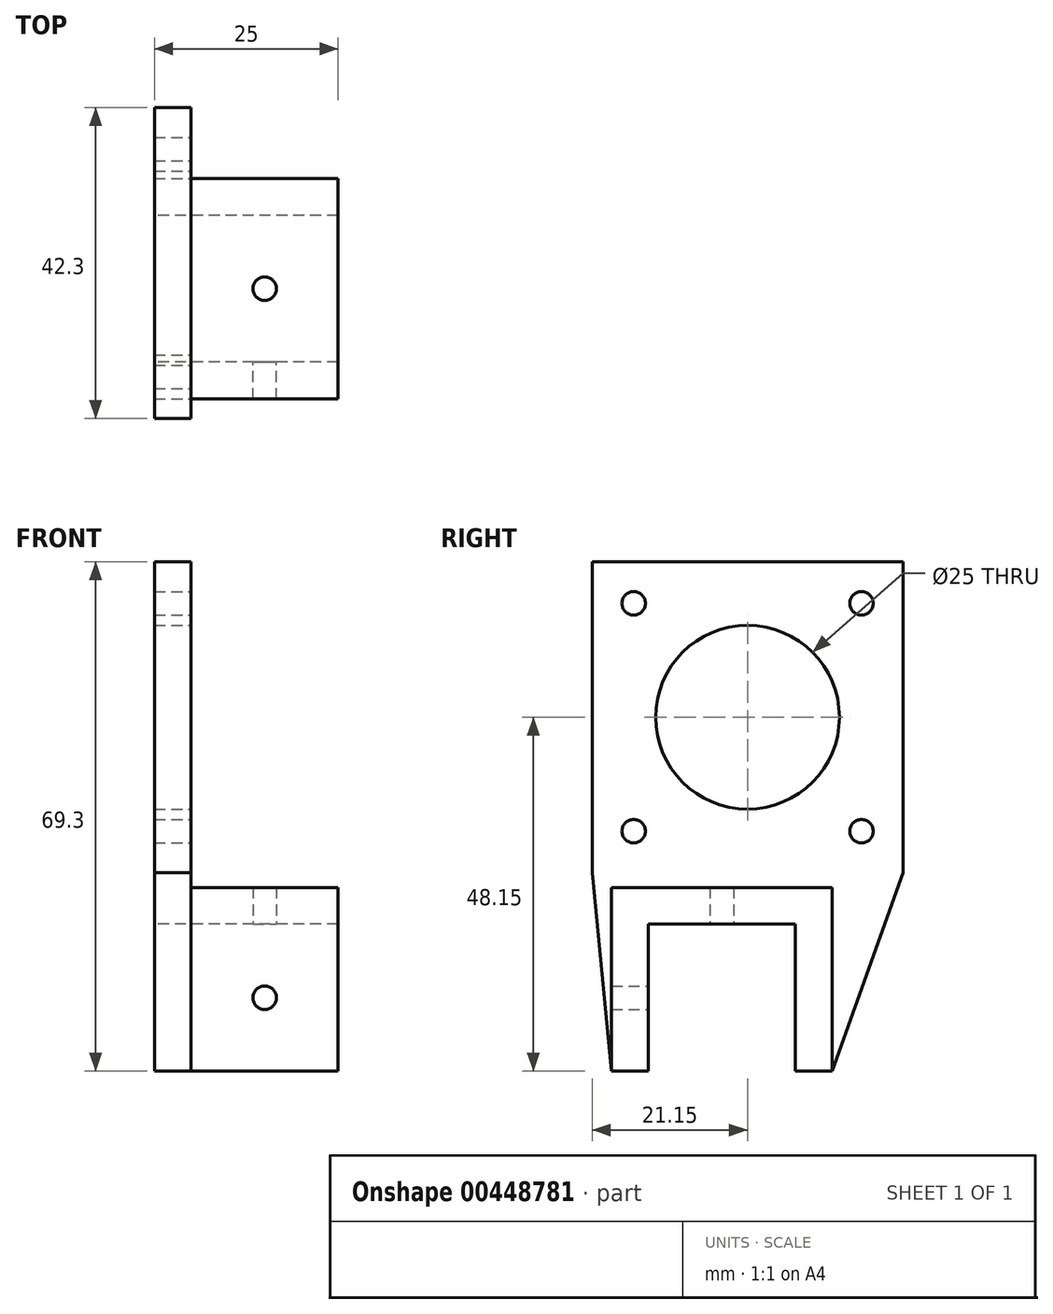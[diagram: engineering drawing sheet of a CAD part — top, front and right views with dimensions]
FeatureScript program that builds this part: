
annotation { "Feature Type Name" : "Feature", "Feature Type Description" : "" }
export const myFeature = defineFeature(function(context is Context, id is Id, definition is map)
    precondition{}
    {
        {
            var Q0;
            Q0=qCreatedBy(makeId("Front.planeOp"),FACE);
            var sketch = newSketch(context, id + "F0", { "sketchPlane" : qUnion([Q0])});
            skLineSegment(sketch, "E0.bottom", {"start": v(0, 0) * mm, "end": v(20, 0) * mm});
            skLineSegment(sketch, "E0.top", {"start": v(0, 25) * mm, "end": v(20, 25) * mm});
            skLineSegment(sketch, "E0.left", {"start": v(0, 0) * mm, "end": v(0, 25) * mm});
            skLineSegment(sketch, "E0.right", {"start": v(20, 0) * mm, "end": v(20, 25) * mm});
            skPoint(sketch, "E1.centerSnap0", {"position": v(0, 12.5) * mm});
            skPoint(sketch, "E1.centerSnap1", {"position": v(10, 0) * mm});
            skSolve(sketch);
        }
        {
            var Q0;
            Q0=makeQuery(id+"F0.imprint","IMPRINT",FACE,{"disambiguationData":[TD([[makeQuery(id+"F0.imprint","IMPRINT",EDGE,{"derivedFrom":sQuery(id+"F0.wireOp",EDGE,"E0.bottom")}),1.0]])]});
            extrude(context, id + "F1", {"entities" : qUnion([Q0]), "depth" : 5 * mm});
        }
        {
            var Q0;
            Q0=makeQuery(id+"F1.opExtrude","CAP_FACE",FACE,{"disambiguationData":[OSD([sQuery(id+"F0.wireOp",EDGE,"E0.bottom"),sQuery(id+"F0.wireOp",EDGE,"E0.top"),sQuery(id+"F0.wireOp",EDGE,"E0.left"),sQuery(id+"F0.wireOp",EDGE,"E0.right"),sQuery(id+"F0.wireOp",EDGE,"E1")])],"isStart":true});
            var sketch = newSketch(context, id + "F2", { "sketchPlane" : qUnion([Q0])});
            skLineSegment(sketch, "E2.bottom", {"start": v(-20, 25) * mm, "end": v(0, 25) * mm});
            skLineSegment(sketch, "E2.top", {"start": v(-20, 20) * mm, "end": v(0, 20) * mm});
            skLineSegment(sketch, "E2.left", {"start": v(-20, 25) * mm, "end": v(-20, 20) * mm});
            skLineSegment(sketch, "E2.right", {"start": v(0, 25) * mm, "end": v(0, 20) * mm});
            skSolve(sketch);
        }
        {
            var Q0;
            Q0=makeQuery(id+"F2.imprint","IMPRINT",FACE,{"disambiguationData":[TD([[makeQuery(id+"F2.imprint","IMPRINT",EDGE,{"derivedFrom":sQuery(id+"F2.wireOp",EDGE,"E2.bottom")}),1.0]])]});
            extrude(context, id + "F3", {"entities" : qUnion([Q0]), "operationType" : NewBodyOperationType.ADD, "depth" : 20 * mm});
        }
        {
            var Q0;
            Q0=makeQuery(id+"F1.opExtrude","CAP_FACE",FACE,{"disambiguationData":[OSD([sQuery(id+"F0.wireOp",EDGE,"E0.bottom"),sQuery(id+"F0.wireOp",EDGE,"E0.top"),sQuery(id+"F0.wireOp",EDGE,"E0.left"),sQuery(id+"F0.wireOp",EDGE,"E0.right")])],"isStart":true});
            var sketch = newSketch(context, id + "F4", { "sketchPlane" : qUnion([Q0])});
            skPoint(sketch, "E3", {"position": v(-10, 10) * mm});
            skPoint(sketch, "E3.positionSnap0", {"position": v(-10, 0) * mm});
            skPoint(sketch, "E3.positionSnap1", {"position": v(0, 10) * mm});
            skSolve(sketch);
        }
        {
            var Q0;
            Q0=makeQuery(id+"F3.opExtrude","SWEPT_FACE",FACE,{"disambiguationData":[OSD([sQuery(id+"F2.wireOp",EDGE,"E2.top")])]});
            var sketch = newSketch(context, id + "F5", { "sketchPlane" : qUnion([Q0])});
            skPoint(sketch, "E4", {"position": v(10, -10) * mm});
            skPoint(sketch, "E4.positionSnap0", {"position": v(10, 0) * mm});
            skPoint(sketch, "E4.positionSnap1", {"position": v(0, -10) * mm});
            skSolve(sketch);
        }
        {
            var Q0;
            Q0=sQuery(id+"F4.wireOp",VERTEX,"E3");
            var Q1;
            Q1=sQuery(id+"F5.wireOp",VERTEX,"E4");
            var Q2;
            Q2=makeQuery(id+"F1.opExtrude","SWEPT_BODY",BODY,{"disambiguationData":[OSD([sQuery(id+"F0.wireOp",EDGE,"E0.bottom"),sQuery(id+"F0.wireOp",EDGE,"E0.top"),sQuery(id+"F0.wireOp",EDGE,"E0.left"),sQuery(id+"F0.wireOp",EDGE,"E0.right")])]});
            hole(context, id + "F6", {"style" : HoleStyle.SIMPLE, "endStyle" : HoleEndStyle.THROUGH, "holeDiameter" : 3.2 * mm, "locations" : qUnion([Q0, Q1]), "scope" : qUnion([Q2]), "isTappedThrough" : true});
        }
        {
            var Q0;
            Q0=makeQuery(id+"F3.boolean.opBoolean","MERGE",FACE,{"derivedFrom":[makeQuery(id+"F1.opExtrude","SWEPT_FACE",FACE,{"disambiguationData":[OSD([sQuery(id+"F0.wireOp",EDGE,"E0.top")])]}),makeQuery(id+"F3.opExtrude","SWEPT_FACE",FACE,{"disambiguationData":[OSD([sQuery(id+"F2.wireOp",EDGE,"E2.bottom")])]})]});
            var sketch = newSketch(context, id + "F7", { "sketchPlane" : qUnion([Q0])});
            skLineSegment(sketch, "E5.bottom", {"start": v(0, 20) * mm, "end": v(20, 20) * mm});
            skLineSegment(sketch, "E5.top", {"start": v(0, 25) * mm, "end": v(20, 25) * mm});
            skLineSegment(sketch, "E5.left", {"start": v(0, 20) * mm, "end": v(0, 25) * mm});
            skLineSegment(sketch, "E5.right", {"start": v(20, 20) * mm, "end": v(20, 25) * mm});
            skSolve(sketch);
        }
        {
            var Q0;
            Q0=makeQuery(id+"F7.imprint","IMPRINT",FACE,{"disambiguationData":[TD([[makeQuery(id+"F7.imprint","IMPRINT",EDGE,{"derivedFrom":sQuery(id+"F7.wireOp",EDGE,"E5.bottom")}),1.0]])]});
            extrude(context, id + "F8", {"entities" : qUnion([Q0]), "operationType" : NewBodyOperationType.ADD, "oppositeDirection" : true, "depth" : 25 * mm});
        }
        {
            var Q0;
            Q0=makeQuery(id+"F3.boolean.opBoolean","MERGE",FACE,{"derivedFrom":[makeQuery(id+"F1.opExtrude","SWEPT_FACE",FACE,{"disambiguationData":[OSD([sQuery(id+"F0.wireOp",EDGE,"E0.left")])]}),makeQuery(id+"F3.opExtrude","SWEPT_FACE",FACE,{"disambiguationData":[OSD([sQuery(id+"F2.wireOp",EDGE,"E2.right")])]})]});
            var sketch = newSketch(context, id + "F9", { "sketchPlane" : qUnion([Q0])});
            skLineSegment(sketch, "E6.bottom", {"start": v(2, 63.65) * mm, "end": v(-29, 63.65) * mm, "construction": true});
            skLineSegment(sketch, "E6.top", {"start": v(2, 32.65) * mm, "end": v(-29, 32.65) * mm, "construction": true});
            skLineSegment(sketch, "E6.left", {"start": v(2, 63.65) * mm, "end": v(2, 32.65) * mm, "construction": true});
            skLineSegment(sketch, "E6.right", {"start": v(-29, 63.65) * mm, "end": v(-29, 32.65) * mm, "construction": true});
            skCircle(sketch, "E7", {"center": v(2, 63.65) * mm, "radius": 1.6 * mm});
            skCircle(sketch, "E8", {"center": v(-29, 63.65) * mm, "radius": 1.6 * mm});
            skCircle(sketch, "E9", {"center": v(-29, 32.65) * mm, "radius": 1.6 * mm});
            skCircle(sketch, "E10", {"center": v(2, 32.65) * mm, "radius": 1.6 * mm});
            skCircle(sketch, "E11", {"center": v(-13.5, 48.15) * mm, "radius": 12.5 * mm});
            skPoint(sketch, "E11.centerSnap0", {"position": v(2, 48.15) * mm});
            skPoint(sketch, "E11.centerSnap1", {"position": v(-13.5, 63.65) * mm});
            skLineSegment(sketch, "E12.bottom", {"start": v(7.65, 69.3) * mm, "end": v(-34.65, 69.3) * mm});
            skLineSegment(sketch, "E12.top", {"start": v(7.65, 27) * mm, "end": v(-34.65, 27) * mm, "construction": true});
            skLineSegment(sketch, "E12.left", {"start": v(7.65, 69.3) * mm, "end": v(7.65, 27) * mm});
            skLineSegment(sketch, "E12.right", {"start": v(-34.65, 69.3) * mm, "end": v(-34.65, 27) * mm});
            skLineSegment(sketch, "E13", {"start": v(-20, 20) * mm, "end": v(0, 20) * mm});
            skLineSegment(sketch, "E14", {"start": v(0, 20) * mm, "end": v(0, 0) * mm});
            skLineSegment(sketch, "E15", {"start": v(0, 0) * mm, "end": v(5, 0) * mm});
            skLineSegment(sketch, "E16", {"start": v(5, 0) * mm, "end": v(7.65, 27) * mm});
            skLineSegment(sketch, "E17", {"start": v(-34.65, 27) * mm, "end": v(-25, 0) * mm});
            skLineSegment(sketch, "E18", {"start": v(-25, 0) * mm, "end": v(-20, 0) * mm});
            skLineSegment(sketch, "E19", {"start": v(-20, 0) * mm, "end": v(-20, 20) * mm});
            skSolve(sketch);
        }
        {
            var Q0;
            Q0=qSketchRegion(id+"F9",true);
            extrude(context, id + "F10", {"entities" : qUnion([Q0]), "operationType" : NewBodyOperationType.ADD, "depth" : 5 * mm});
        }
    });
